# Revit family: Integrated_Sink-Two_Station-Sloan-AER_DEC-AD-82000
name_source: partatom
category: Plumbing Fixtures
revit_build: Autodesk Revit 2014 (Build: 20130308_1515(x64)
units: mm (PartAtom-declared; Revit-internal decimal feet)

## types (1)
- AD-82000
    ADA Compliant = Yes
    Assembly Code = D2010610
    CW Connection = Yes
    CWFU = 1.5
    Cold Water Connection Radius = 1/4"
    Default Elevation = 34"
    Description = Two Station AER-DEC Integrated Sink
    HW Connection = Yes
    HWFU = 1.5
    Hot Water Connection Radius = 1/4"
    IAPMO Certification = cUPC
    Manufacturer = Sloan Valve Company
    Material = Stone-Sloan-DuPont Corian Solid Surface
    Model = AD-82000
    Mounting = Wall Mounted
    Operation = Sensor-Activated
    Price = Prices may vary. Please consult Manufacturer Representative for most up-to-date price list.
    Product Documentation Link = https://specifications.sloan.com
    Product Page URL = https://www.sloan.com
    URL = http://www.sloan.com
    Vent Connection = No
    WFU = 2
    Warrenty = 3 Year Limited
    Waste Connection = Yes
    Waste Connection Radius = 3/4"
    Width = 60"

## geometry (parser evidence)
native form markers: Sweep x7
no freeform markers — native parametric forms only
